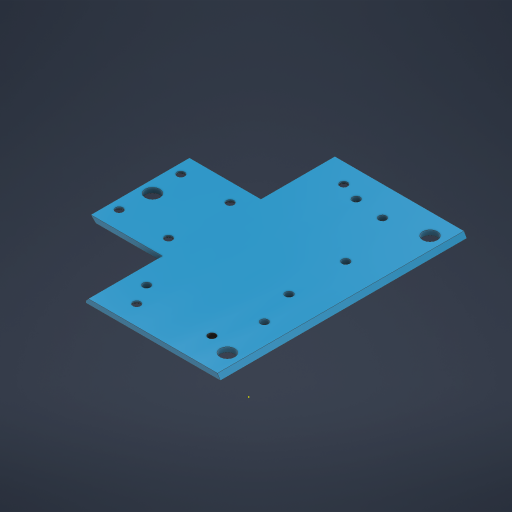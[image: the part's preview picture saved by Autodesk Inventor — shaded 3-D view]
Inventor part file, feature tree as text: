
AUTODESK INVENTOR PART (.ipt)
format: ipt  version: 2024 (Build 280153000, 153)  size: 297,984 bytes
history: native  units: in
note: dims shown in document units (in); Inventor stores cm internally (conversion verified against a paired STEP export)
features: sketch x8, hole x5, chamfer x4, extrude x2, plane x1, projected_geometry x1
ambient origin geometry x8: Origin, YZ Plane, XZ Plane, XY Plane, X Axis, Y Axis, Z Axis, Center Point
bodies: Solid1 (feature_tree)
feature tree (21):
  extrude  "Extrusion1"  Depth=1.1811in
  plane  "Work Plane1"
  hole  "Hole1"  [1 undecoded]
  chamfer  "Chamfer1"  Distance=0.0787in Angle=45.0deg
  chamfer  "Chamfer2"  Distance=0.0787in Angle=45.0deg
  extrude  "Extrusion2"  Depth=0.2362in
  chamfer  "Chamfer3"  Distance=4.7244in
  hole  "Hole2"  [1 undecoded]
  chamfer  "Chamfer4"  Distance=1.6512in
  hole  "Hole3"  [1 undecoded]
  sketch  "Sketch7"  dims[d27=3.7008in d28=0.0394in d29=0.0472in d30=45.0deg]
  hole  "Hole4"  [1 undecoded]
  hole  "Hole6"  [1 undecoded]
  sketch  "Sketch1"  dims[d0=3.937in d2=1.1811in]
  sketch  "Sketch2"  dims[d4=1.5748in d5=0.0787in d6=0.0in]
  sketch  "Sketch3"  dims[d7=2.5984in]
  sketch  "Sketch4"  dims[d9=0.122in d10=0.2362in d11=0.1575in d12=0.0787in d13=90.0deg d14=0.315in d15=0.8108in d16=0.0591in d17=0.0787in d18=45.0deg d19=0.0787in d20=0.0787in d21=45.0deg]
  sketch  "Sketch6"  dims[d22=0.315in d23=120.0deg d24=0.2362in d25=4.7244in d26=0.0in]
  projected_geometry  "Projected Loop1"
  sketch  "Sketch8"  dims[d31=0.315in]
  sketch  "Sketch10"  dims[d32=1.6512in d33=1.6512in d34=0.315in d35=3.937in d36=0.122in d37=0.2362in d38=0.1575in d39=0.0787in d40=90.0deg d41=0.315in d42=0.8108in d43=0.0591in d44=0.0787in d45=45.0deg d46=0.122in d47=0.2362in d48=0.1575in d49=0.0787in d50=90.0deg d51=0.315in d52=0.8108in d56=1.3661in d57=1.664in d61=0.2362in d62=0.2362in d63=0.1575in d64=0.0787in d65=90.0deg d66=0.315in d67=0.8108in d75=0.122in d76=0.2362in d77=0.1575in d78=0.0787in d79=90.0deg d80=0.315in d81=0.8108in d83=0.8302in d84=0.4724in d85=0.4724in d87=0.5619in d88=0.5674in d89=0.5674in d91=0.382in d92=1.0848in d53=0.0295in d54=0.8108in d55=0.0025in]
note: 5 required parameter values undecoded (feature->parameter linkage not recoverable at this tier; creation-order binding heuristic only, values carry confidence <= 0.55)
